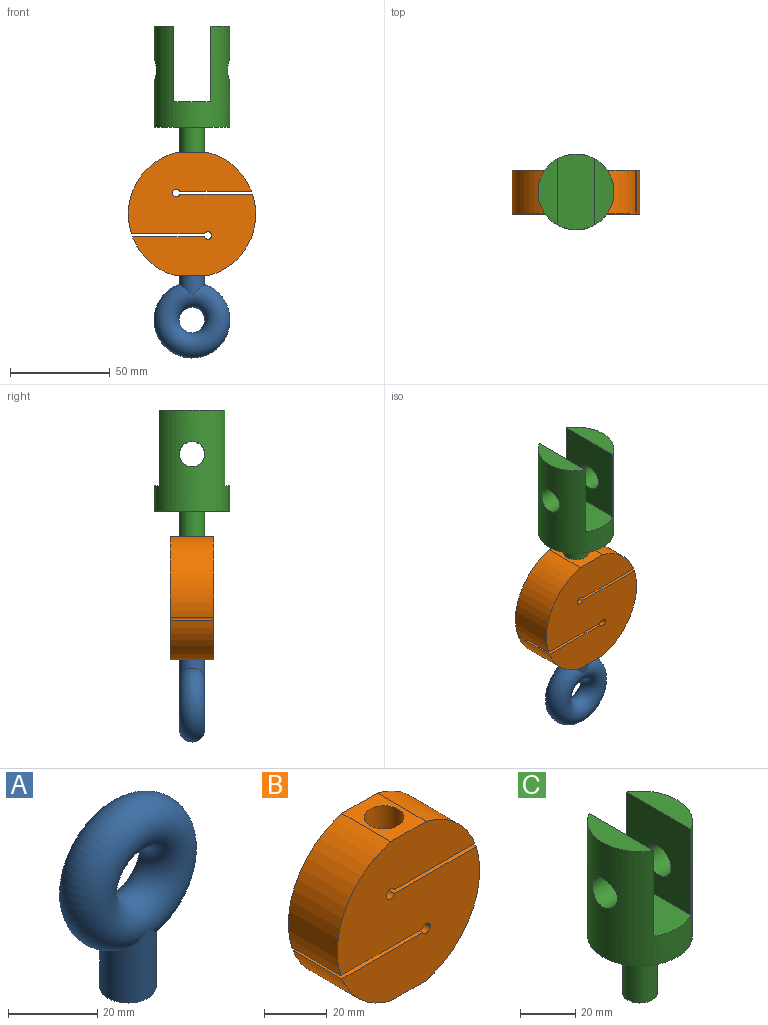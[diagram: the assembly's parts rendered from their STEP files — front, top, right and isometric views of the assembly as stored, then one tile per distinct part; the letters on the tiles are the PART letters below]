
ASSEMBLY  parts=3 mates=2
PART A: 3 faces, bbox 41.2x12.7x52.4 mm
  f0: cylinder r=6.35mm len=19.05mm, axis (0,0,1), area 621.6mm2, adj f1,f2
  f1: plane 12.7x12.7mm, normal (0,0,-1), area 126.7mm2, adj f0
  f2: torus R=12.7mm, axis (0,1,0), area 3020.1mm2, adj f0
PART B: 18 faces, bbox 64x22x62 mm
  f0: cylinder r=32mm len=22mm, axis (0,1,0), area 672.2mm2, adj f2,f3,f6,f13
  f1: cylinder r=32mm len=22mm, axis (0,1,0), area 672.2mm2, adj f2,f3,f4,f15
  f2: plane 64x62mm, normal (0,-1,0), area 3064.2mm2, adj f0,f1,f4,f5,f6,f7,f12,f13
  f3: plane 64x62mm, normal (0,1,0), area 3064.2mm2, adj f0,f1,f4,f5,f6,f7,f12,f13
  f4: plane 22x15.87mm, normal (0,0,1), area 222.6mm2, adj f1,f2,f3,f5,f8
  f5: cylinder r=32mm len=40.93mm, axis (0,1,0), area 1151.5mm2, adj f2,f3,f4,f12
  f6: plane 22x15.87mm, normal (0,0,-1), area 222.6mm2, adj f0,f2,f3,f7,f10
  f7: cylinder r=32mm len=40.93mm, axis (0,1,0), area 1151.5mm2, adj f2,f3,f6,f17
  f8: cylinder r=6.35mm len=19.05mm, axis (0,0,1), area 760.1mm2, adj f4,f9
  f9: plane 12.7x12.7mm, normal (0,0,1), area 126.7mm2, adj f8
  f10: cylinder r=6.35mm len=19.05mm, axis (0,0,-1), area 760.1mm2, adj f6,f11
  f11: plane 12.7x12.7mm, normal (0,0,-1), area 126.7mm2, adj f10
  f12: plane 36.61x22mm, normal (0,0,-1), area 805.3mm2, adj f2,f3,f5,f14
  f13: plane 36.08x22mm, normal (0,0,1), area 793.7mm2, adj f0,f2,f3,f14
  f14: cylinder r=1.91mm len=22mm, axis (0,-1,0), area 229.4mm2, adj f2,f3,f12,f13
  f15: plane 36.08x22mm, normal (0,0,-1), area 793.7mm2, adj f1,f2,f3,f16
  f16: cylinder r=1.91mm len=22mm, axis (0,-1,0), area 229.4mm2, adj f2,f3,f15,f17
  f17: plane 36.61x22mm, normal (0,0,1), area 805.3mm2, adj f2,f3,f7,f16
PART C: 11 faces, bbox 38.1x38.1x76.2 mm
  f0: plane 33x9.53mm, normal (0,0,1), area 222.9mm2, adj f1,f4
  f1: cylinder r=19.05mm len=50.8mm, axis (0,0,-1), area 4303.5mm2, adj f0,f2,f3,f4,f5,f6,f7,f8
  f2: plane 33x9.53mm, normal (0,0,1), area 222.9mm2, adj f1,f5
  f3: plane 38.1x38.1mm, normal (0,0,-1), area 1013.4mm2, adj f1,f9
  f4: plane 38.1x33mm, normal (-1,0,0), area 1130.5mm2, adj f0,f1,f6,f8
  f5: plane 38.1x33mm, normal (1,0,0), area 1130.5mm2, adj f1,f2,f6,f7
  f6: plane 38.1x19.05mm, normal (0,0,1), area 694.3mm2, adj f1,f4,f5
  f7: cylinder r=6.35mm len=12.7mm, axis (1,0,0), area 358.5mm2, adj f1,f5
  f8: cylinder r=6.35mm len=12.7mm, axis (1,0,0), area 358.4mm2, adj f1,f4
  f9: cylinder r=6.35mm len=25.4mm, axis (0,0,1), area 1013.4mm2, adj f3,f10
  f10: plane 12.7x12.7mm, normal (0,0,-1), area 126.7mm2, adj f9
PLACE A rot(axis=(1,0,0),180deg) t=(0,-11,-40.47)mm
PLACE B at identity
PLACE C t=(0,-11,43.7)mm
MATE cylindrical A.f0 <-> B.f8  axis (0,0,-1) through (0,-11,-31)mm
MATE cylindrical C.f9 <-> B.f8  axis (0,0,1) through (0,-11,31)mm
